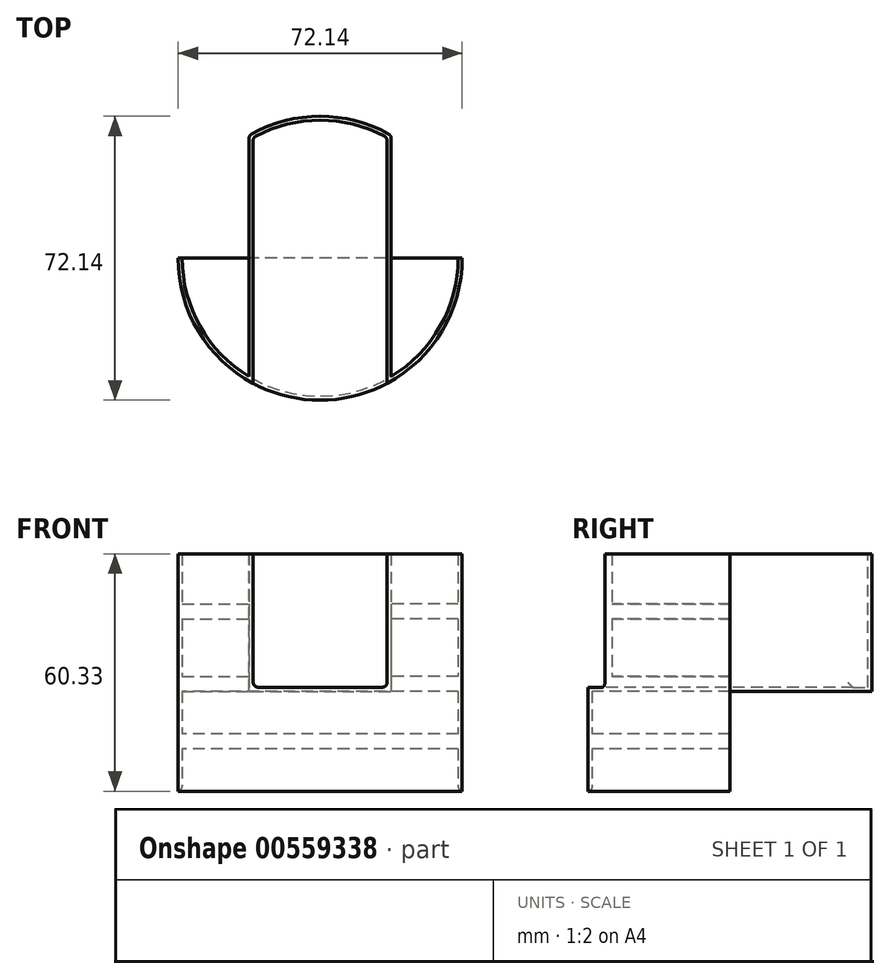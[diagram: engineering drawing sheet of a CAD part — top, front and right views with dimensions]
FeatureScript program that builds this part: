
annotation { "Feature Type Name" : "Feature", "Feature Type Description" : "" }
export const myFeature = defineFeature(function(context is Context, id is Id, definition is map)
    precondition{}
    {
        {
            var Q0;
            Q0=qCreatedBy(makeId("Top.planeOp"),FACE);
            var sketch = newSketch(context, id + "F0", { "sketchPlane" : qUnion([Q0])});
            skArc(sketch, "E0", {"start": v(-36.07, 0) * mm, "mid": v(0, -36.07) * mm, "end": v(36.07, 0) * mm});
            skArc(sketch, "E1", {"start": v(-35.05, 0) * mm, "mid": v(0, -35.05) * mm, "end": v(35.05, 0) * mm});
            skLineSegment(sketch, "E2", {"start": v(-36.07, 0) * mm, "end": v(-35.05, 0) * mm});
            skLineSegment(sketch, "E3.trimOffspring", {"start": v(35.05, 0) * mm, "end": v(36.07, 0) * mm});
            skSolve(sketch);
        }
        {
            var Q0;
            Q0 = qSketchRegion(id + "F0", true);
            extrude(context, id + "F1", {"entities" : qUnion([Q0]), "depth" : 120.65 * mm, "offsetDistance" : 25.4 * mm});
        }
        {
            var Q0;
            Q0=qCreatedBy(makeId("Front.planeOp"),FACE);
            cPlane(context, id + "F2", {"entities" : qUnion([Q0]), "cplaneType" : CPlaneType.OFFSET, "offset" : 36.07 * mm, "width" : 152.4 * mm, "height" : 152.4 * mm});
        }
        {
            var Q0;
            Q0=qCreatedBy(id+"F2.planeOp",FACE);
            var sketch = newSketch(context, id + "F3", { "sketchPlane" : qUnion([Q0])});
            skLineSegment(sketch, "E4.bottom", {"start": v(-18.03, 95.25) * mm, "end": v(18.03, 95.25) * mm});
            skLineSegment(sketch, "E4.top", {"start": v(-18.03, 25.4) * mm, "end": v(18.03, 25.4) * mm});
            skLineSegment(sketch, "E4.left", {"start": v(-18.03, 95.25) * mm, "end": v(-18.03, 25.4) * mm});
            skLineSegment(sketch, "E4.right", {"start": v(18.03, 95.25) * mm, "end": v(18.03, 25.4) * mm});
            skSolve(sketch);
        }
        {
            var Q0;
            Q0 = qSketchRegion(id + "F3", true);
            extrude(context, id + "F4", {"entities" : qUnion([Q0]), "operationType" : NewBodyOperationType.ADD, "oppositeDirection" : true, "depth" : 72.14 * mm, "offsetDistance" : 25.4 * mm});
        }
        {
            var Q0;
            Q0=makeQuery(id+"F4.opExtrude","CAP_FACE",FACE,{"disambiguationData":[OSD([sQuery(id+"F3.wireOp",EDGE,"E4.bottom"),sQuery(id+"F3.wireOp",EDGE,"E4.top"),sQuery(id+"F3.wireOp",EDGE,"E4.left"),sQuery(id+"F3.wireOp",EDGE,"E4.right")])],"isStart":true});
            shell(context, id + "F5", {"entities" : qUnion([Q0]), "thickness" : 1.02 * mm});
        }
        {
            var Q0;
            Q0=makeQuery(id+"F1.opExtrude","CAP_FACE",FACE,{"disambiguationData":[OSD([sQuery(id+"F0.wireOp",EDGE,"E0"),sQuery(id+"F0.wireOp",EDGE,"E1"),sQuery(id+"F0.wireOp",EDGE,"E2"),sQuery(id+"F0.wireOp",EDGE,"E3.trimOffspring")])],"isStart":false});
            var sketch = newSketch(context, id + "F6", { "sketchPlane" : qUnion([Q0])});
            skCircle(sketch, "E5", {"center": v(0, 0) * mm, "radius": 36.07 * mm});
            skCircle(sketch, "E6", {"center": v(0, 0) * mm, "radius": 87.59 * mm});
            skSolve(sketch);
        }
        {
            var Q0;
            Q0 = qSketchRegion(id + "F6", true);
            extrude(context, id + "F7", {"entities" : qUnion([Q0]), "operationType" : NewBodyOperationType.REMOVE, "endBound" : BoundingType.THROUGH_ALL, "oppositeDirection" : true, "depth" : 25.4 * mm, "offsetDistance" : 25.4 * mm});
        }
        {
            var Q0;
            {var subQ0=sQuery(id+"F3.wireOp",EDGE,"E4.left");var subQ1=sQuery(id+"F3.wireOp",EDGE,"E4.right");var subQ2=sQuery(id+"F3.wireOp",EDGE,"E4.bottom");Q0=makeQuery(id+"F4.boolean.opBoolean","SPLIT",FACE,{"disambiguationData":[TD([makeQuery(id+"F1.opExtrude","SWEPT_FACE",FACE,{"disambiguationData":[OSD([sQuery(id+"F0.wireOp",EDGE,"E1")])]}),makeQuery(id+"F4.opExtrude","CAP_FACE",FACE,{"disambiguationData":[OSD([subQ2,sQuery(id+"F3.wireOp",EDGE,"E4.top"),subQ0,subQ1])],"isStart":false}),makeQuery(id+"F4.opExtrude","SWEPT_FACE",FACE,{"disambiguationData":[OSD([subQ0])]}),makeQuery(id+"F4.opExtrude","SWEPT_FACE",FACE,{"disambiguationData":[OSD([subQ1])]})])],"derivedFrom":makeQuery(id+"F4.opExtrude","SWEPT_FACE",FACE,{"disambiguationData":[OSD([subQ2])]})});}
            var sketch = newSketch(context, id + "F8", { "sketchPlane" : qUnion([Q0])});
            skArc(sketch, "E7", {"start": v(18.03, 31.24) * mm, "mid": v(0, 36.07) * mm, "end": v(-18.03, 31.24) * mm});
            skArc(sketch, "E8.0", {"start": v(17.53, 30.36) * mm, "mid": v(0, 35.05) * mm, "end": v(-17.53, 30.36) * mm});
            skLineSegment(sketch, "E9", {"start": v(-18.03, 31.24) * mm, "end": v(-17.53, 30.36) * mm});
            skLineSegment(sketch, "E10", {"start": v(18.03, 31.24) * mm, "end": v(17.53, 30.36) * mm});
            skSolve(sketch);
        }
        {
            var Q0;
            Q0 = qSketchRegion(id + "F8", true);
            var Q1;
            Q1=makeQuery(id+"F5.opShell","OFFSET_FACE",FACE,{"disambiguationData":[OSD([sQuery(id+"F3.wireOp",EDGE,"E4.top")])]});
            extrude(context, id + "F9", {"entities" : qUnion([Q0]), "operationType" : NewBodyOperationType.ADD, "endBound" : BoundingType.UP_TO_SURFACE, "oppositeDirection" : true, "depth" : 25.4 * mm, "endBoundEntityFace" : qUnion([Q1]), "offsetDistance" : 25.4 * mm});
        }
        {
            var Q0;
            Q0=qCreatedBy(id+"F2.planeOp",FACE);
            var sketch = newSketch(context, id + "F10", { "sketchPlane" : qUnion([Q0])});
            skLineSegment(sketch, "E11.bottom", {"start": v(-42.79, 120.65) * mm, "end": v(57.17, 120.65) * mm});
            skLineSegment(sketch, "E11.top", {"start": v(-42.79, 60.32) * mm, "end": v(57.17, 60.32) * mm});
            skLineSegment(sketch, "E11.left", {"start": v(-42.79, 120.65) * mm, "end": v(-42.79, 60.32) * mm});
            skLineSegment(sketch, "E11.right", {"start": v(57.17, 120.65) * mm, "end": v(57.17, 60.32) * mm});
            skSolve(sketch);
        }
        {
            var Q0;
            Q0 = qSketchRegion(id + "F10", true);
            extrude(context, id + "F11", {"entities" : qUnion([Q0]), "operationType" : NewBodyOperationType.REMOVE, "endBound" : BoundingType.THROUGH_ALL, "oppositeDirection" : true, "depth" : 25.4 * mm, "offsetDistance" : 25.4 * mm});
        }
        {
            var Q0;
            Q0=qCreatedBy(makeId("Front.planeOp"),FACE);
            var sketch = newSketch(context, id + "F12", { "sketchPlane" : qUnion([Q0])});
            skLineSegment(sketch, "E12.bottom", {"start": v(35.05, 47.62) * mm, "end": v(18.03, 47.62) * mm});
            skLineSegment(sketch, "E12.top", {"start": v(35.05, 43.81) * mm, "end": v(18.03, 43.81) * mm});
            skLineSegment(sketch, "E12.left", {"start": v(35.05, 47.62) * mm, "end": v(35.05, 43.81) * mm});
            skLineSegment(sketch, "E12.right", {"start": v(18.03, 47.62) * mm, "end": v(18.03, 43.81) * mm});
            skLineSegment(sketch, "E13.bottom", {"start": v(35.05, 29.21) * mm, "end": v(18.03, 29.21) * mm});
            skLineSegment(sketch, "E13.top", {"start": v(35.05, 25.4) * mm, "end": v(18.03, 25.4) * mm});
            skLineSegment(sketch, "E13.left", {"start": v(35.05, 29.21) * mm, "end": v(35.05, 25.4) * mm});
            skLineSegment(sketch, "E13.right", {"start": v(18.03, 29.21) * mm, "end": v(18.03, 25.4) * mm});
            skLineSegment(sketch, "E14.MirrorCS", {"start": v(-35.05, 25.4) * mm, "end": v(-18.03, 25.4) * mm});
            skLineSegment(sketch, "E15.MirrorCS", {"start": v(-18.03, 29.21) * mm, "end": v(-18.03, 25.4) * mm});
            skLineSegment(sketch, "E16.MirrorCS", {"start": v(-35.05, 29.21) * mm, "end": v(-18.03, 29.21) * mm});
            skLineSegment(sketch, "E17.MirrorCS", {"start": v(-35.05, 29.21) * mm, "end": v(-35.05, 25.4) * mm});
            skLineSegment(sketch, "E18.MirrorCS", {"start": v(-18.03, 47.62) * mm, "end": v(-18.03, 43.81) * mm});
            skLineSegment(sketch, "E19.MirrorCS", {"start": v(-35.05, 43.81) * mm, "end": v(-18.03, 43.81) * mm});
            skLineSegment(sketch, "E20.MirrorCS", {"start": v(-35.05, 47.62) * mm, "end": v(-35.05, 43.81) * mm});
            skLineSegment(sketch, "E21.MirrorCS", {"start": v(-35.05, 47.62) * mm, "end": v(-18.03, 47.62) * mm});
            skLineSegment(sketch, "E22.bottom", {"start": v(35.05, 14.6) * mm, "end": v(-35.05, 14.6) * mm});
            skLineSegment(sketch, "E22.top", {"start": v(35.05, 10.8) * mm, "end": v(-35.05, 10.8) * mm});
            skLineSegment(sketch, "E22.left", {"start": v(35.05, 14.6) * mm, "end": v(35.05, 10.8) * mm});
            skLineSegment(sketch, "E22.right", {"start": v(-35.05, 14.6) * mm, "end": v(-35.05, 10.8) * mm});
            skSolve(sketch);
        }
        {
            var Q0;
            Q0 = qSketchRegion(id + "F12", true);
            extrude(context, id + "F13", {"entities" : qUnion([Q0]), "operationType" : NewBodyOperationType.ADD, "endBound" : BoundingType.UP_TO_NEXT, "depth" : 25.4 * mm, "offsetDistance" : 25.4 * mm});
        }
        {
            var Q0;
            Q0=makeQuery(id+"F9.opExtrude","CAP_EDGE",EDGE,{"disambiguationData":[OSD([sQuery(id+"F8.wireOp",EDGE,"E8.0")])],"isStart":false});
            var Q1;
            Q1=makeQuery(id+"F9.boolean.opBoolean","INTERSECT",EDGE,{"derivedFrom":[makeQuery(id+"F5.opShell","OFFSET_FACE",FACE,{"disambiguationData":[OSD([sQuery(id+"F3.wireOp",EDGE,"E4.left")])]}),makeQuery(id+"F9.opExtrude","SWEPT_FACE",FACE,{"disambiguationData":[OSD([sQuery(id+"F8.wireOp",EDGE,"E8.0")])]})]});
            var Q2;
            Q2=makeQuery(id+"F5.opShell","OFFSET_EDGE",EDGE,{"disambiguationData":[OSD([sQuery(id+"F3.wireOp",EDGE,"E4.top"),sQuery(id+"F3.wireOp",EDGE,"E4.left")])]});
            var Q3;
            Q3=makeQuery(id+"F9.boolean.opBoolean","INTERSECT",EDGE,{"derivedFrom":[makeQuery(id+"F5.opShell","OFFSET_FACE",FACE,{"disambiguationData":[OSD([sQuery(id+"F3.wireOp",EDGE,"E4.right")])]}),makeQuery(id+"F9.opExtrude","SWEPT_FACE",FACE,{"disambiguationData":[OSD([sQuery(id+"F8.wireOp",EDGE,"E8.0")])]})]});
            var Q4;
            Q4=makeQuery(id+"F5.opShell","OFFSET_EDGE",EDGE,{"disambiguationData":[OSD([sQuery(id+"F3.wireOp",EDGE,"E4.top"),sQuery(id+"F3.wireOp",EDGE,"E4.right")])]});
            var Q5;
            Q5=makeQuery(id+"F1.opExtrude","CAP_EDGE",EDGE,{"disambiguationData":[OSD([sQuery(id+"F0.wireOp",EDGE,"E1")])],"isStart":true});
            var Q6;
            {var subQ1=sQuery(id+"F3.wireOp",EDGE,"E4.right");Q6=makeQuery(id+"F7.boolean.opBoolean","INTERSECT",EDGE,{"derivedFrom":[makeQuery(id+"F4.boolean.opBoolean","SPLIT",FACE,{"disambiguationData":[TD([makeQuery(id+"F1.opExtrude","SWEPT_FACE",FACE,{"disambiguationData":[OSD([sQuery(id+"F0.wireOp",EDGE,"E1")])]})])],"derivedFrom":makeQuery(id+"F4.opExtrude","SWEPT_FACE",FACE,{"disambiguationData":[OSD([subQ1])]})}),makeQuery(id+"F7.opExtrude","SWEPT_FACE",FACE,{"disambiguationData":[OSD([sQuery(id+"F6.wireOp",EDGE,"E5")])]})]});}
            fillet(context, id + "F14", {"entities" : qUnion([Q0, Q1, Q2, Q3, Q4, Q5, Q6]), "radius" : 1.27 * mm, "tangentPropagation" : true, "allowEdgeOverflow" : false});
        }
        {
            var Q0;
            {var subQ1=sQuery(id+"F3.wireOp",EDGE,"E4.left");Q0=makeQuery(id+"F7.boolean.opBoolean","INTERSECT",EDGE,{"derivedFrom":[makeQuery(id+"F4.boolean.opBoolean","SPLIT",FACE,{"disambiguationData":[TD([makeQuery(id+"F1.opExtrude","SWEPT_FACE",FACE,{"disambiguationData":[OSD([sQuery(id+"F0.wireOp",EDGE,"E1")])]})])],"derivedFrom":makeQuery(id+"F4.opExtrude","SWEPT_FACE",FACE,{"disambiguationData":[OSD([subQ1])]})}),makeQuery(id+"F7.opExtrude","SWEPT_FACE",FACE,{"disambiguationData":[OSD([sQuery(id+"F6.wireOp",EDGE,"E5")])]})]});}
            fillet(context, id + "F15", {"entities" : qUnion([Q0]), "radius" : 1.27 * mm, "tangentPropagation" : true, "allowEdgeOverflow" : false});
        }
    });
